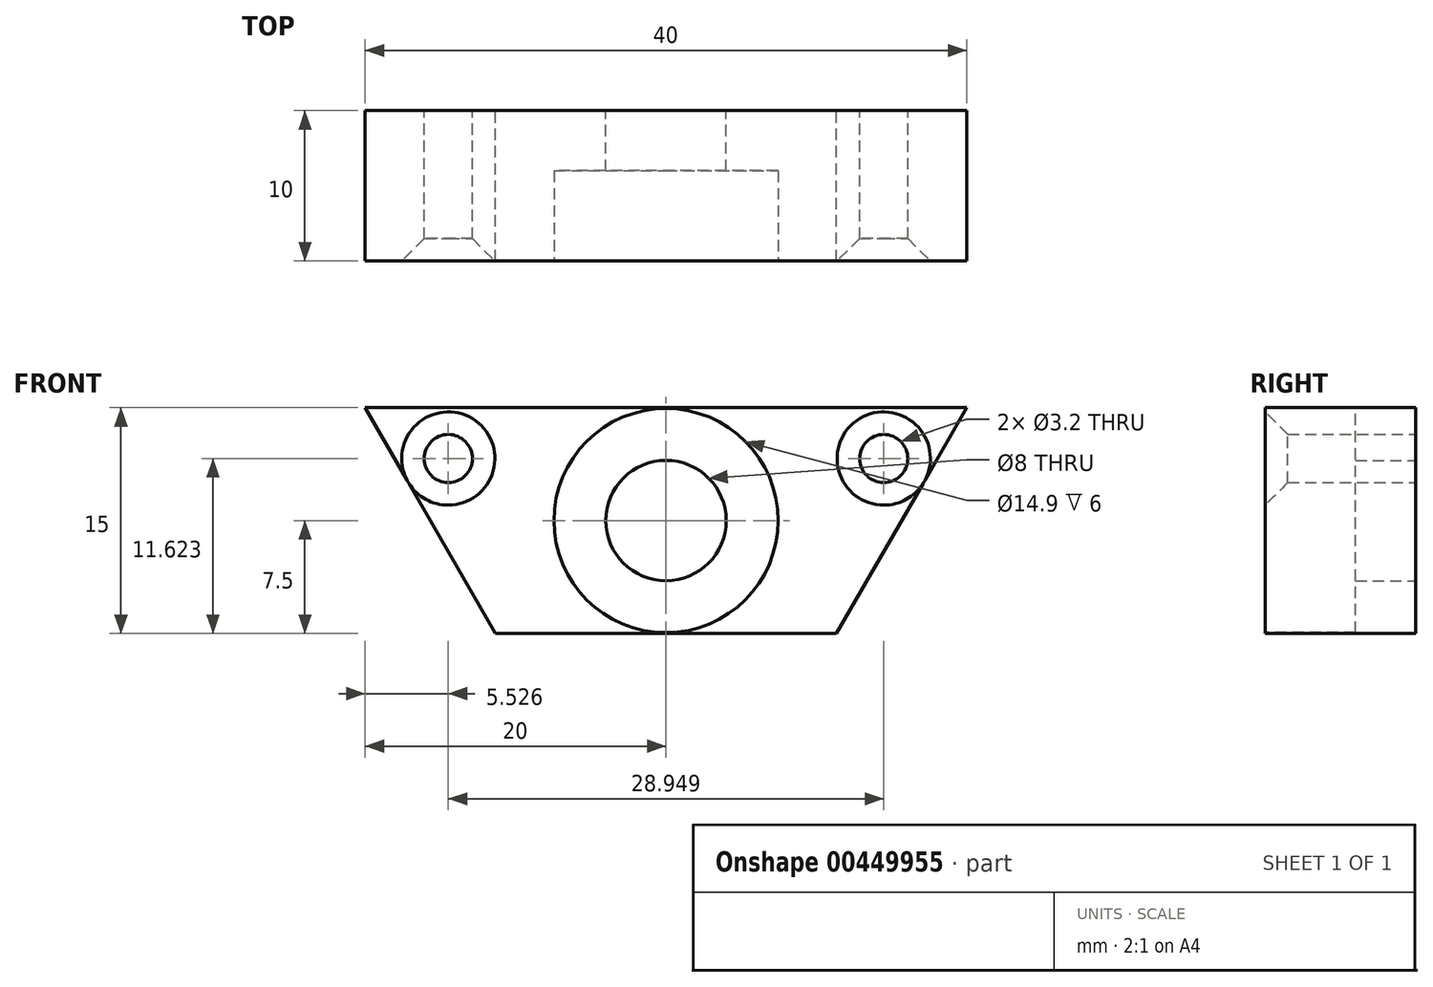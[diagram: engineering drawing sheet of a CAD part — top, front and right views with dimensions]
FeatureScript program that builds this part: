
annotation { "Feature Type Name" : "Feature", "Feature Type Description" : "" }
export const myFeature = defineFeature(function(context is Context, id is Id, definition is map)
    precondition{}
    {
        {
            var Q0;
            Q0=qCreatedBy(makeId("Front.planeOp"),FACE);
            var sketch = newSketch(context, id + "F0", { "sketchPlane" : qUnion([Q0])});
            skLineSegment(sketch, "E0.bottom", {"start": v(-20, 7.5) * mm, "end": v(20, 7.5) * mm});
            skLineSegment(sketch, "E0.top", {"start": v(-11.34, -7.5) * mm, "end": v(11.34, -7.5) * mm});
            skLineSegment(sketch, "E1", {"start": v(-20, 7.5) * mm, "end": v(-11.34, -7.5) * mm});
            skLineSegment(sketch, "E2.MirrorCS", {"start": v(20, 7.5) * mm, "end": v(11.34, -7.5) * mm});
            skPoint(sketch, "E3.orphan", {"position": v(5.49, -17.63) * mm});
            skPoint(sketch, "E4.orphan", {"position": v(-5.49, -17.63) * mm});
            skPoint(sketch, "E0.left.end.orphan", {"position": v(-20, -7.5) * mm});
            skPoint(sketch, "E0.right.end.orphan", {"position": v(20, -7.5) * mm});
            skCircle(sketch, "E5", {"center": v(0, 0) * mm, "radius": 4 * mm});
            skCircle(sketch, "E6", {"center": v(-14.47, 4.12) * mm, "radius": 1.6 * mm});
            skCircle(sketch, "E7.MirrorC", {"center": v(14.47, 4.12) * mm, "radius": 1.6 * mm});
            skSolve(sketch);
        }
        {
            var Q0;
            Q0=makeQuery(id+"F0.imprint","IMPRINT",FACE,{"disambiguationData":[TD([[makeQuery(id+"F0.imprint","IMPRINT",EDGE,{"derivedFrom":sQuery(id+"F0.wireOp",EDGE,"E0.bottom")}),-1.0]])]});
            extrude(context, id + "F1", {"entities" : qUnion([Q0]), "depth" : 10 * mm});
        }
        {
            var Q0;
            Q0=makeQuery(id+"F1.opExtrude","CAP_FACE",FACE,{"disambiguationData":[OSD([sQuery(id+"F0.wireOp",EDGE,"E0.bottom"),sQuery(id+"F0.wireOp",EDGE,"E0.top"),sQuery(id+"F0.wireOp",EDGE,"E1"),sQuery(id+"F0.wireOp",EDGE,"E2.MirrorCS"),sQuery(id+"F0.wireOp",EDGE,"E5"),sQuery(id+"F0.wireOp",EDGE,"E6"),sQuery(id+"F0.wireOp",EDGE,"E7.MirrorC")])],"isStart":false});
            var sketch = newSketch(context, id + "F2", { "sketchPlane" : qUnion([Q0])});
            skCircle(sketch, "E8", {"center": v(0, 0) * mm, "radius": 7.45 * mm});
            skSolve(sketch);
        }
        {
            var Q0;
            Q0=makeQuery(id+"F2.imprint","IMPRINT",FACE,{"disambiguationData":[TD([[makeQuery(id+"F2.imprint","IMPRINT",EDGE,{"derivedFrom":sQuery(id+"F2.wireOp",EDGE,"E8")}),1.0]])]});
            extrude(context, id + "F3", {"entities" : qUnion([Q0]), "operationType" : NewBodyOperationType.REMOVE, "oppositeDirection" : true, "depth" : 6 * mm});
        }
        {
            var Q0;
            Q0=makeQuery(id+"F1.opExtrude","CAP_EDGE",EDGE,{"disambiguationData":[OSD([sQuery(id+"F0.wireOp",EDGE,"E6")])],"isStart":false});
            var Q1;
            Q1=makeQuery(id+"F1.opExtrude","CAP_EDGE",EDGE,{"disambiguationData":[OSD([sQuery(id+"F0.wireOp",EDGE,"E7.MirrorC")])],"isStart":false});
            chamfer(context, id + "F4", {"entities" : qUnion([Q0, Q1]), "width" : 1.5 * mm, "tangentPropagation" : true});
        }
    });
